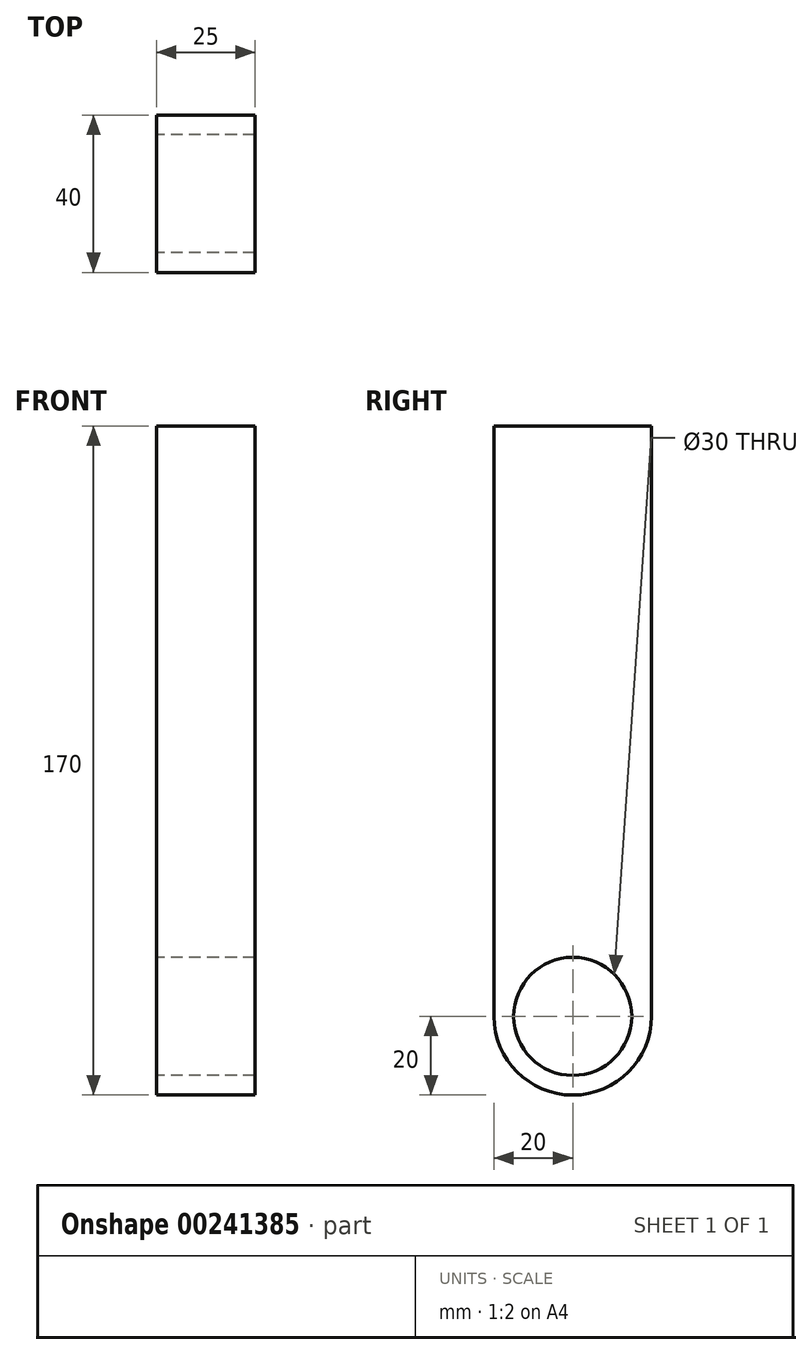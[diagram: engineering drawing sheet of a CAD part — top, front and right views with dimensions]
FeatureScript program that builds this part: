
annotation { "Feature Type Name" : "Feature", "Feature Type Description" : "" }
export const myFeature = defineFeature(function(context is Context, id is Id, definition is map)
    precondition{}
    {
        {
            var Q0;
            Q0=qCreatedBy(makeId("Right.planeOp"),FACE);
            var sketch = newSketch(context, id + "F0", { "sketchPlane" : qUnion([Q0])});
            skLineSegment(sketch, "E0.bottom", {"start": v(-20, 0) * mm, "end": v(20, 0) * mm});
            skLineSegment(sketch, "E0.top", {"start": v(-20, 150) * mm, "end": v(20, 150) * mm});
            skLineSegment(sketch, "E0.left", {"start": v(-20, 0) * mm, "end": v(-20, 150) * mm});
            skLineSegment(sketch, "E0.right", {"start": v(20, 0) * mm, "end": v(20, 150) * mm});
            skCircle(sketch, "E1", {"center": v(0, 0) * mm, "radius": 20 * mm});
            skCircle(sketch, "E2", {"center": v(0, 0) * mm, "radius": 15 * mm});
            skSolve(sketch);
        }
        {
            var Q0;
            Q0 = qSketchRegion(id + "F0", true);
            extrude(context, id + "F1", {"entities" : qUnion([Q0]), "depth" : 25 * mm});
        }
    });
